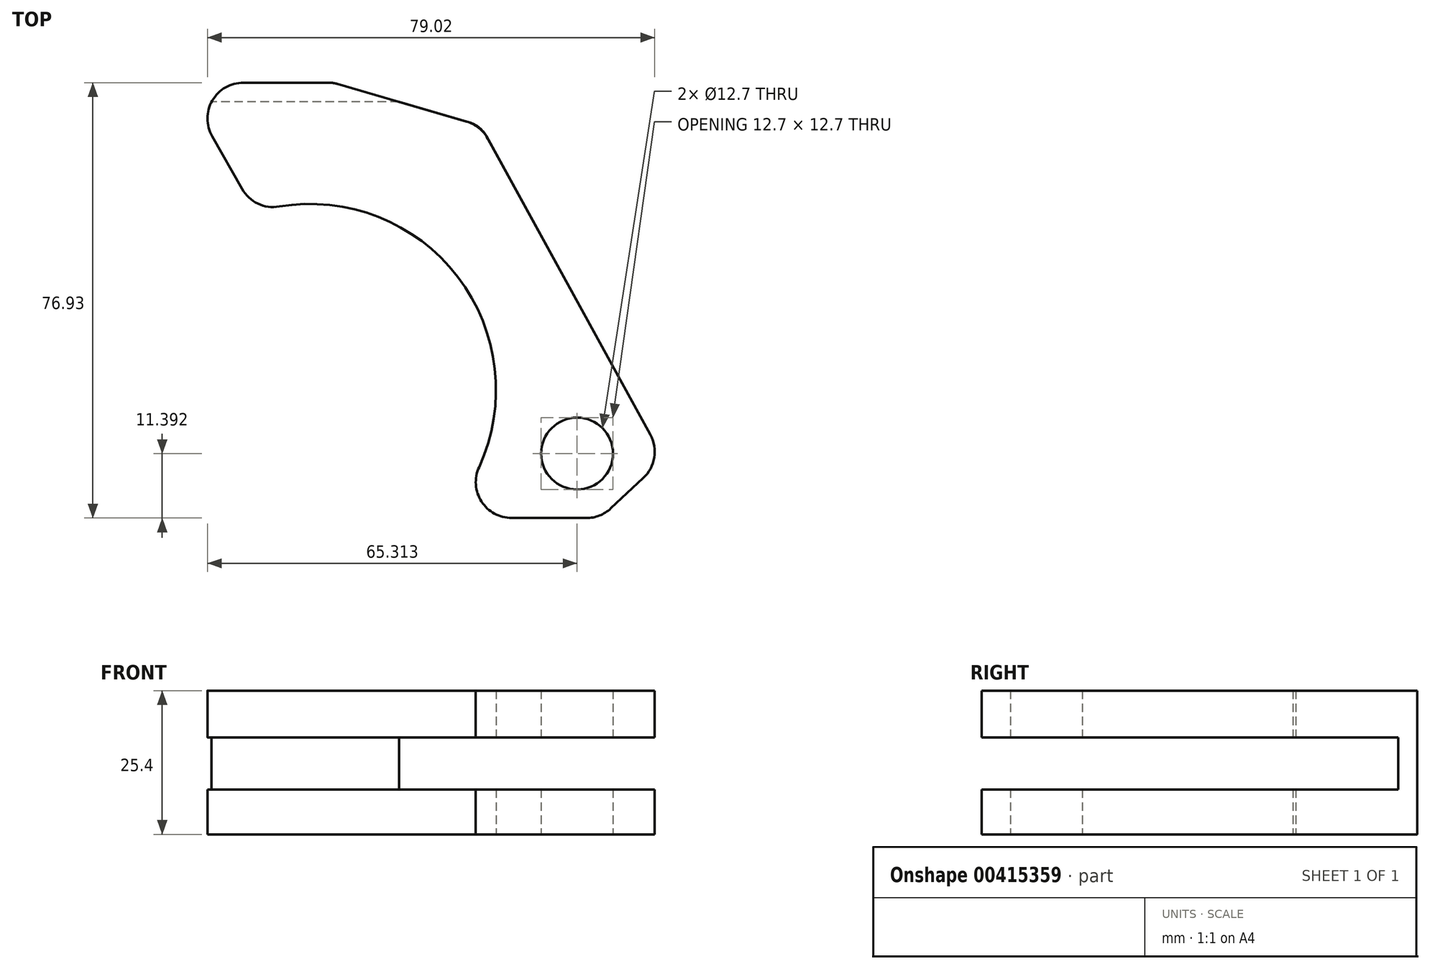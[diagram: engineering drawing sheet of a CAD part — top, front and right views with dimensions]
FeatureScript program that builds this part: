
annotation { "Feature Type Name" : "Feature", "Feature Type Description" : "" }
export const myFeature = defineFeature(function(context is Context, id is Id, definition is map)
    precondition{}
    {
        {
            var Q0;
            Q0=qCreatedBy(makeId("Top.planeOp"),FACE);
            var sketch = newSketch(context, id + "F0", { "sketchPlane" : qUnion([Q0])});
            skLineSegment(sketch, "E0", {"start": v(-25.44, 24.94) * mm, "end": v(-38.46, 47.84) * mm});
            skLineSegment(sketch, "E1", {"start": v(-38.46, 47.84) * mm, "end": v(-11.66, 47.84) * mm});
            skLineSegment(sketch, "E2", {"start": v(-11.66, 47.84) * mm, "end": v(14.38, 40.24) * mm});
            skLineSegment(sketch, "E3", {"start": v(14.38, 40.24) * mm, "end": v(46.71, -18.67) * mm});
            skLineSegment(sketch, "E4", {"start": v(46.71, -18.67) * mm, "end": v(35.54, -29.1) * mm});
            skLineSegment(sketch, "E5", {"start": v(35.54, -29.1) * mm, "end": v(7.98, -29.1) * mm});
            skArc(sketch, "E6", {"start": v(7.98, -29.1) * mm, "mid": v(12.17, 10.86) * mm, "end": v(-25.44, 24.94) * mm});
            skCircle(sketch, "E7", {"center": v(31.41, -17.7) * mm, "radius": 6.35 * mm});
            skSolve(sketch);
        }
        {
            var Q0;
            Q0 = qSketchRegion(id + "F0", true);
            extrude(context, id + "F1", {"entities" : qUnion([Q0]), "depth" : 25.4 * mm});
        }
        {
            var Q0;
            Q0=qCreatedBy(makeId("Front.planeOp"),FACE);
            var sketch = newSketch(context, id + "F2", { "sketchPlane" : qUnion([Q0])});
            skLineSegment(sketch, "E8.bottom", {"start": v(67.06, 7.94) * mm, "end": v(-56.26, 7.94) * mm});
            skLineSegment(sketch, "E8.top", {"start": v(67.06, 17.15) * mm, "end": v(-56.26, 17.15) * mm});
            skLineSegment(sketch, "E8.left", {"start": v(67.06, 7.94) * mm, "end": v(67.06, 17.15) * mm});
            skLineSegment(sketch, "E8.right", {"start": v(-56.26, 7.94) * mm, "end": v(-56.26, 17.15) * mm});
            skSolve(sketch);
        }
        {
            var Q0;
            Q0 = qSketchRegion(id + "F2", true);
            extrude(context, id + "F3", {"entities" : qUnion([Q0]), "operationType" : NewBodyOperationType.REMOVE, "endBound" : BoundingType.SYMMETRIC, "depth" : 88.9 * mm});
        }
        {
            var Q0;
            {var subQ0=sQuery(id+"F0.wireOp",EDGE,"E3");var subQ1=sQuery(id+"F0.wireOp",EDGE,"E2");Q0=makeQuery(id+"F3.boolean.opBoolean","SPLIT",EDGE,{"disambiguationData":[TD([makeQuery(id+"F3.opExtrude","SWEPT_FACE",FACE,{"disambiguationData":[OSD([sQuery(id+"F2.wireOp",EDGE,"E8.top")])]})])],"derivedFrom":makeQuery(id+"F1.opExtrude","SWEPT_EDGE",EDGE,{"disambiguationData":[OSD([subQ1,subQ0])]})});}
            fillet(context, id + "F4", {"entities" : qUnion([Q0]), "radius" : 6.35 * mm, "tangentPropagation" : true, "allowEdgeOverflow" : false});
        }
        {
            var Q0;
            {var subQ0=sQuery(id+"F0.wireOp",EDGE,"E3");var subQ1=sQuery(id+"F0.wireOp",EDGE,"E2");Q0=makeQuery(id+"F3.boolean.opBoolean","SPLIT",EDGE,{"disambiguationData":[TD([makeQuery(id+"F3.opExtrude","SWEPT_FACE",FACE,{"disambiguationData":[OSD([sQuery(id+"F2.wireOp",EDGE,"E8.bottom")])]})])],"derivedFrom":makeQuery(id+"F1.opExtrude","SWEPT_EDGE",EDGE,{"disambiguationData":[OSD([subQ1,subQ0])]})});}
            fillet(context, id + "F5", {"entities" : qUnion([Q0]), "radius" : 5.08 * mm, "tangentPropagation" : true, "allowEdgeOverflow" : false});
        }
        {
            var Q0;
            Q0=makeQuery(id+"F1.opExtrude","SWEPT_EDGE",EDGE,{"disambiguationData":[OSD([sQuery(id+"F0.wireOp",EDGE,"E1"),sQuery(id+"F0.wireOp",EDGE,"E2")])]});
            fillet(context, id + "F6", {"entities" : qUnion([Q0]), "radius" : 5.08 * mm, "tangentPropagation" : true, "allowEdgeOverflow" : false});
        }
        {
            var Q0;
            {var subQ0=sQuery(id+"F0.wireOp",EDGE,"E6");var subQ1=sQuery(id+"F0.wireOp",EDGE,"E5");Q0=makeQuery(id+"F3.boolean.opBoolean","SPLIT",EDGE,{"disambiguationData":[TD([makeQuery(id+"F3.opExtrude","SWEPT_FACE",FACE,{"disambiguationData":[OSD([sQuery(id+"F2.wireOp",EDGE,"E8.top")])]})])],"derivedFrom":makeQuery(id+"F1.opExtrude","SWEPT_EDGE",EDGE,{"disambiguationData":[OSD([subQ1,subQ0])]})});}
            var Q1;
            {var subQ0=sQuery(id+"F0.wireOp",EDGE,"E6");var subQ1=sQuery(id+"F0.wireOp",EDGE,"E5");Q1=makeQuery(id+"F3.boolean.opBoolean","SPLIT",EDGE,{"disambiguationData":[TD([makeQuery(id+"F3.opExtrude","SWEPT_FACE",FACE,{"disambiguationData":[OSD([sQuery(id+"F2.wireOp",EDGE,"E8.bottom")])]})])],"derivedFrom":makeQuery(id+"F1.opExtrude","SWEPT_EDGE",EDGE,{"disambiguationData":[OSD([subQ1,subQ0])]})});}
            fillet(context, id + "F7", {"entities" : qUnion([Q0, Q1]), "radius" : 6.35 * mm, "tangentPropagation" : true, "allowEdgeOverflow" : false});
        }
        {
            var Q0;
            {var subQ0=sQuery(id+"F0.wireOp",EDGE,"E5");var subQ1=sQuery(id+"F0.wireOp",EDGE,"E4");Q0=makeQuery(id+"F3.boolean.opBoolean","SPLIT",EDGE,{"disambiguationData":[TD([makeQuery(id+"F3.opExtrude","SWEPT_FACE",FACE,{"disambiguationData":[OSD([sQuery(id+"F2.wireOp",EDGE,"E8.bottom")])]})])],"derivedFrom":makeQuery(id+"F1.opExtrude","SWEPT_EDGE",EDGE,{"disambiguationData":[OSD([subQ1,subQ0])]})});}
            var Q1;
            {var subQ0=sQuery(id+"F0.wireOp",EDGE,"E5");var subQ1=sQuery(id+"F0.wireOp",EDGE,"E4");Q1=makeQuery(id+"F3.boolean.opBoolean","SPLIT",EDGE,{"disambiguationData":[TD([makeQuery(id+"F3.opExtrude","SWEPT_FACE",FACE,{"disambiguationData":[OSD([sQuery(id+"F2.wireOp",EDGE,"E8.top")])]})])],"derivedFrom":makeQuery(id+"F1.opExtrude","SWEPT_EDGE",EDGE,{"disambiguationData":[OSD([subQ1,subQ0])]})});}
            var Q2;
            {var subQ0=sQuery(id+"F0.wireOp",EDGE,"E4");var subQ1=sQuery(id+"F0.wireOp",EDGE,"E3");Q2=makeQuery(id+"F3.boolean.opBoolean","SPLIT",EDGE,{"disambiguationData":[TD([makeQuery(id+"F3.opExtrude","SWEPT_FACE",FACE,{"disambiguationData":[OSD([sQuery(id+"F2.wireOp",EDGE,"E8.top")])]})])],"derivedFrom":makeQuery(id+"F1.opExtrude","SWEPT_EDGE",EDGE,{"disambiguationData":[OSD([subQ1,subQ0])]})});}
            var Q3;
            {var subQ0=sQuery(id+"F0.wireOp",EDGE,"E4");var subQ1=sQuery(id+"F0.wireOp",EDGE,"E3");Q3=makeQuery(id+"F3.boolean.opBoolean","SPLIT",EDGE,{"disambiguationData":[TD([makeQuery(id+"F3.opExtrude","SWEPT_FACE",FACE,{"disambiguationData":[OSD([sQuery(id+"F2.wireOp",EDGE,"E8.bottom")])]})])],"derivedFrom":makeQuery(id+"F1.opExtrude","SWEPT_EDGE",EDGE,{"disambiguationData":[OSD([subQ1,subQ0])]})});}
            fillet(context, id + "F8", {"entities" : qUnion([Q0, Q1, Q2, Q3]), "radius" : 6.35 * mm, "tangentPropagation" : true, "allowEdgeOverflow" : false});
        }
        {
            var Q0;
            {var subQ0=sQuery(id+"F0.wireOp",EDGE,"E0");var subQ1=sQuery(id+"F0.wireOp",EDGE,"E6");Q0=makeQuery(id+"F3.boolean.opBoolean","SPLIT",EDGE,{"disambiguationData":[TD([makeQuery(id+"F3.opExtrude","SWEPT_FACE",FACE,{"disambiguationData":[OSD([sQuery(id+"F2.wireOp",EDGE,"E8.bottom")])]})])],"derivedFrom":makeQuery(id+"F1.opExtrude","SWEPT_EDGE",EDGE,{"disambiguationData":[OSD([subQ0,subQ1])]})});}
            var Q1;
            {var subQ0=sQuery(id+"F0.wireOp",EDGE,"E0");var subQ1=sQuery(id+"F0.wireOp",EDGE,"E6");Q1=makeQuery(id+"F3.boolean.opBoolean","SPLIT",EDGE,{"disambiguationData":[TD([makeQuery(id+"F3.opExtrude","SWEPT_FACE",FACE,{"disambiguationData":[OSD([sQuery(id+"F2.wireOp",EDGE,"E8.top")])]})])],"derivedFrom":makeQuery(id+"F1.opExtrude","SWEPT_EDGE",EDGE,{"disambiguationData":[OSD([subQ0,subQ1])]})});}
            var Q2;
            Q2=makeQuery(id+"F1.opExtrude","SWEPT_EDGE",EDGE,{"disambiguationData":[OSD([sQuery(id+"F0.wireOp",EDGE,"E0"),sQuery(id+"F0.wireOp",EDGE,"E1")])]});
            fillet(context, id + "F9", {"entities" : qUnion([Q0, Q1, Q2]), "radius" : 6.35 * mm, "tangentPropagation" : true, "allowEdgeOverflow" : false});
        }
    });
